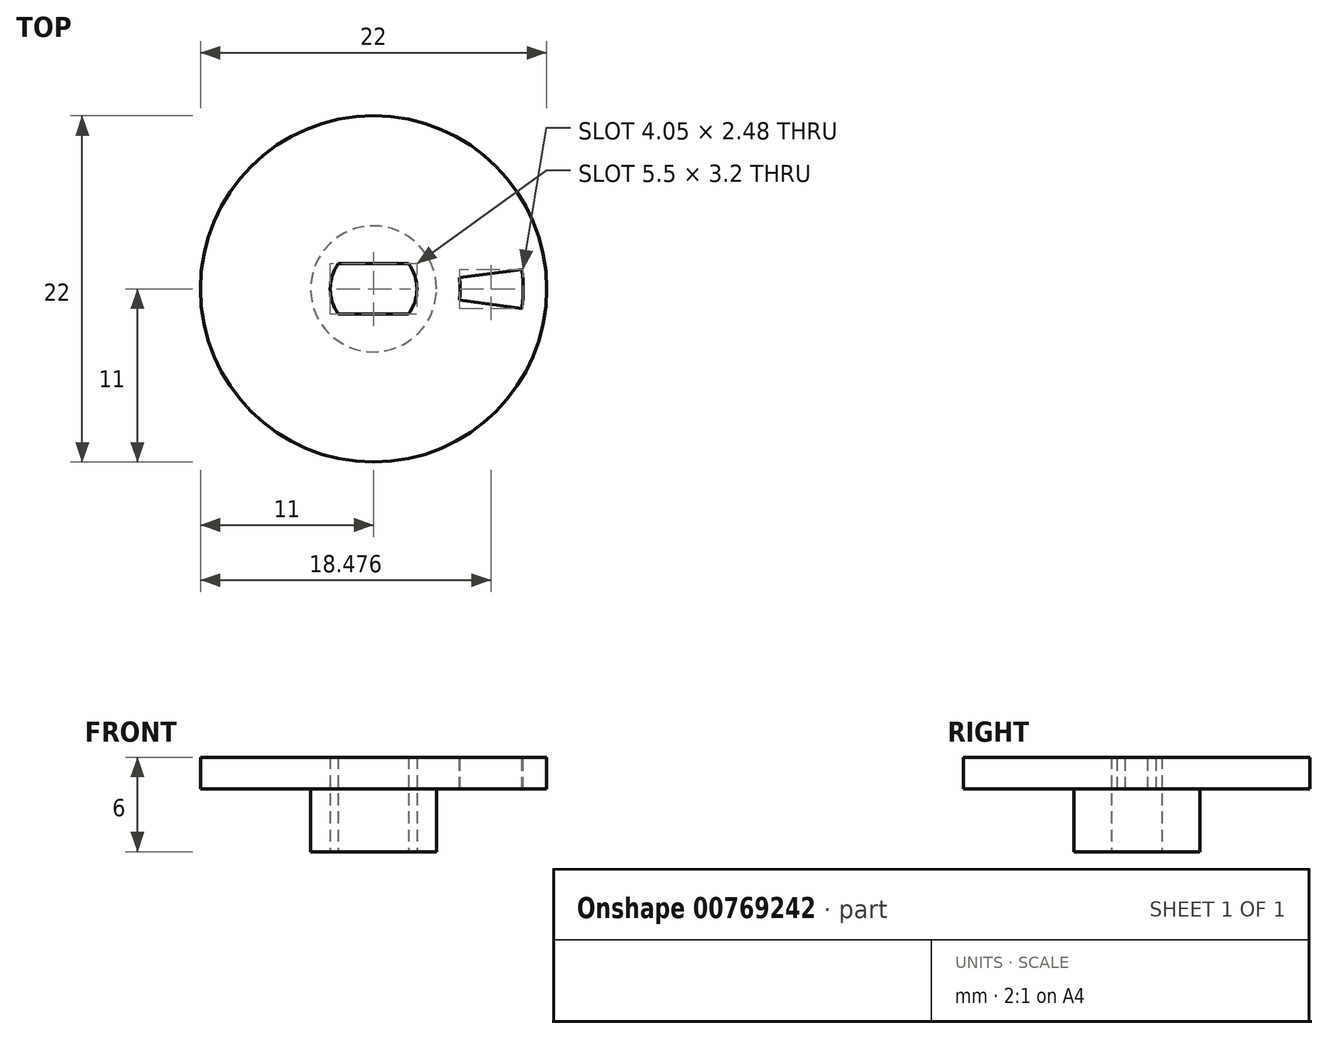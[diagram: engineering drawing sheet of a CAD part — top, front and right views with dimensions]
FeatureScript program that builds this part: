
annotation { "Feature Type Name" : "Feature", "Feature Type Description" : "" }
export const myFeature = defineFeature(function(context is Context, id is Id, definition is map)
    precondition{}
    {
        {
            var Q0;
            Q0=qCreatedBy(makeId("Top.planeOp"),FACE);
            var sketch = newSketch(context, id + "F0", { "sketchPlane" : qUnion([Q0])});
            skCircle(sketch, "E0", {"center": v(0, 0) * mm, "radius": 11 * mm});
            skSolve(sketch);
        }
        {
            var Q0;
            Q0=makeQuery(id+"F0.imprint","IMPRINT",FACE,{"disambiguationData":[TD([[makeQuery(id+"F0.imprint","IMPRINT",EDGE,{"derivedFrom":sQuery(id+"F0.wireOp",EDGE,"E0")}),1.0]])]});
            extrude(context, id + "F1", {"entities" : qUnion([Q0]), "depth" : 2 * mm, "offsetDistance" : 25 * mm});
        }
        {
            var Q0;
            Q0=makeQuery(id+"F1.opExtrude","CAP_FACE",FACE,{"disambiguationData":[OSD([sQuery(id+"F0.wireOp",EDGE,"E0")])],"isStart":false});
            var sketch = newSketch(context, id + "F2", { "sketchPlane" : qUnion([Q0])});
            skLineSegment(sketch, "E1.bottom", {"start": v(5.45, 0.72) * mm, "end": v(9.42, 1.24) * mm});
            skLineSegment(sketch, "E1.top", {"start": v(5.45, -0.72) * mm, "end": v(9.42, -1.24) * mm});
            skArc(sketch, "E2", {"start": v(5.45, -0.72) * mm, "mid": v(5.5, 0) * mm, "end": v(5.45, 0.72) * mm});
            skArc(sketch, "E3", {"start": v(9.42, -1.24) * mm, "mid": v(9.5, 0) * mm, "end": v(9.42, 1.24) * mm});
            skLineSegment(sketch, "E4", {"start": v(0, 0) * mm, "end": v(5.45, 0.72) * mm, "construction": true});
            skLineSegment(sketch, "E5", {"start": v(0, 0) * mm, "end": v(5.45, -0.72) * mm, "construction": true});
            skSolve(sketch);
        }
        {
            var Q0;
            Q0 = qSketchRegion(id + "F2", true);
            extrude(context, id + "F3", {"entities" : qUnion([Q0]), "operationType" : NewBodyOperationType.REMOVE, "oppositeDirection" : true, "depth" : 2 * mm, "offsetDistance" : 25 * mm});
        }
        {
            var Q0;
            Q0=makeQuery(id+"F1.opExtrude","CAP_FACE",FACE,{"disambiguationData":[OSD([sQuery(id+"F0.wireOp",EDGE,"E0")])],"isStart":true});
            var sketch = newSketch(context, id + "F4", { "sketchPlane" : qUnion([Q0])});
            skCircle(sketch, "E6", {"center": v(0, 0) * mm, "radius": 4 * mm});
            skSolve(sketch);
        }
        {
            var Q0;
            Q0 = qSketchRegion(id + "F4", true);
            extrude(context, id + "F5", {"entities" : qUnion([Q0]), "operationType" : NewBodyOperationType.ADD, "depth" : 4 * mm, "offsetDistance" : 25 * mm});
        }
        {
            var Q0;
            Q0=makeQuery(id+"F5.opExtrude","CAP_FACE",FACE,{"disambiguationData":[OSD([sQuery(id+"F4.wireOp",EDGE,"E6")])],"isStart":false});
            var sketch = newSketch(context, id + "F6", { "sketchPlane" : qUnion([Q0])});
            skArc(sketch, "E7", {"start": v(2.24, -1.6) * mm, "mid": v(2.75, 0) * mm, "end": v(2.24, 1.6) * mm});
            skArc(sketch, "E8", {"start": v(-2.24, 1.6) * mm, "mid": v(-2.75, 0) * mm, "end": v(-2.24, -1.6) * mm});
            skLineSegment(sketch, "E9", {"start": v(-2.24, 1.6) * mm, "end": v(2.24, 1.6) * mm});
            skLineSegment(sketch, "E10", {"start": v(2.24, -1.6) * mm, "end": v(-2.24, -1.6) * mm});
            skSolve(sketch);
        }
        {
            var Q0;
            Q0 = qSketchRegion(id + "F6", true);
            extrude(context, id + "F7", {"entities" : qUnion([Q0]), "operationType" : NewBodyOperationType.REMOVE, "oppositeDirection" : true, "depth" : 9 * mm, "offsetDistance" : 25 * mm});
        }
    });
